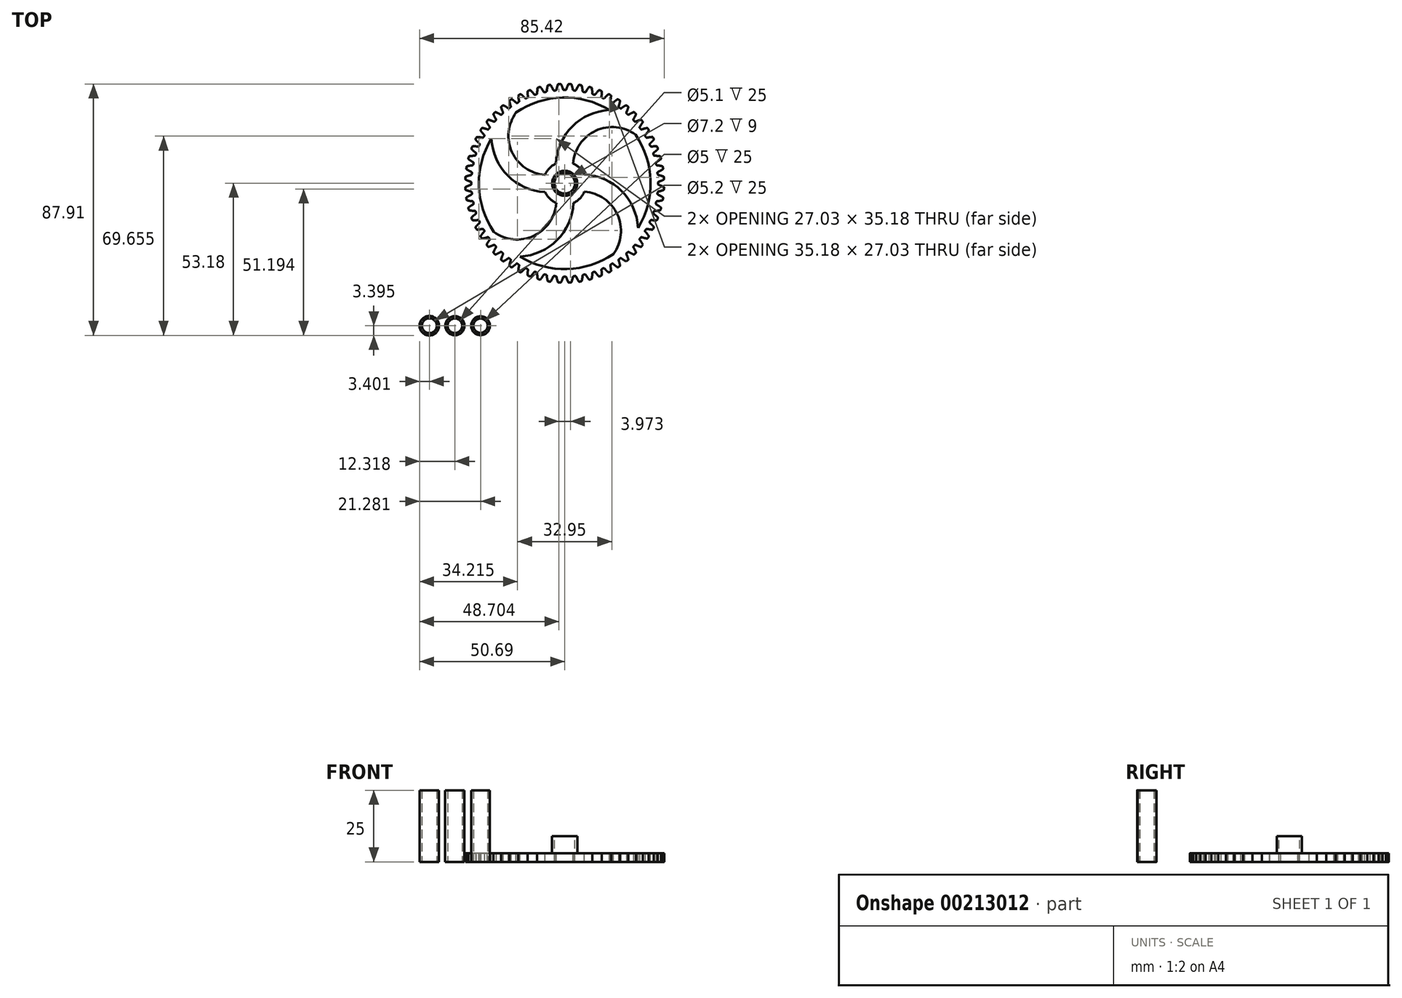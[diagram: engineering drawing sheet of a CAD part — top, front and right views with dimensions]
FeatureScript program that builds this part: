
annotation { "Feature Type Name" : "Feature", "Feature Type Description" : "" }
export const myFeature = defineFeature(function(context is Context, id is Id, definition is map)
    precondition{}
    {
        {
            var Q0;
            Q0=qCreatedBy(makeId("Top.planeOp"),FACE);
            var sketch = newSketch(context, id + "F0", { "sketchPlane" : qUnion([Q0])});
            skCircle(sketch, "E0", {"center": v(0, 0) * mm, "radius": 31.71 * mm, "construction": true});
            skLineSegment(sketch, "E1", {"start": v(0, 0) * mm, "end": v(31.71, 0) * mm, "construction": true});
            skLineSegment(sketch, "E2", {"start": v(31.71, 0) * mm, "end": v(31.71, 0) * mm});
            skLineSegment(sketch, "E3", {"start": v(0, 0) * mm, "end": v(31.68, 1.5) * mm, "construction": true});
            skLineSegment(sketch, "E4", {"start": v(31.68, 1.5) * mm, "end": v(31.75, 0) * mm, "construction": true});
            skLineSegment(sketch, "E5", {"start": v(0, 0) * mm, "end": v(31.57, 2.98) * mm, "construction": true});
            skLineSegment(sketch, "E6", {"start": v(31.57, 2.98) * mm, "end": v(31.86, 0) * mm, "construction": true});
            skLineSegment(sketch, "E7", {"start": v(0, 0) * mm, "end": v(31.4, 4.47) * mm, "construction": true});
            skLineSegment(sketch, "E8", {"start": v(31.4, 4.47) * mm, "end": v(32.03, 0.03) * mm, "construction": true});
            skLineSegment(sketch, "E9", {"start": v(0, 0) * mm, "end": v(31.15, 5.94) * mm, "construction": true});
            skLineSegment(sketch, "E10", {"start": v(31.15, 5.94) * mm, "end": v(32.27, 0.07) * mm, "construction": true});
            skLineSegment(sketch, "E11", {"start": v(0, 0) * mm, "end": v(30.84, 7.4) * mm, "construction": true});
            skLineSegment(sketch, "E12", {"start": v(30.84, 7.4) * mm, "end": v(32.58, 0.14) * mm, "construction": true});
            skLineSegment(sketch, "E13", {"start": v(0, 0) * mm, "end": v(30.46, 8.85) * mm, "construction": true});
            skLineSegment(sketch, "E14", {"start": v(30.46, 8.85) * mm, "end": v(32.96, 0.24) * mm, "construction": true});
            skLineSegment(sketch, "E15", {"start": v(0, 0) * mm, "end": v(30, 10.27) * mm, "construction": true});
            skLineSegment(sketch, "E16", {"start": v(30, 10.27) * mm, "end": v(33.4, 0.38) * mm, "construction": true});
            skLineSegment(sketch, "E17", {"start": v(0, 0) * mm, "end": v(29.49, 11.67) * mm, "construction": true});
            skLineSegment(sketch, "E18", {"start": v(29.49, 11.67) * mm, "end": v(33.89, 0.56) * mm, "construction": true});
            skLineSegment(sketch, "E19", {"start": v(0, 0) * mm, "end": v(28.9, 13.05) * mm, "construction": true});
            skLineSegment(sketch, "E20", {"start": v(28.9, 13.05) * mm, "end": v(34.44, 0.8) * mm, "construction": true});
            skLineSegment(sketch, "E21", {"start": v(0, 0) * mm, "end": v(28.26, 14.4) * mm, "construction": true});
            skLineSegment(sketch, "E22", {"start": v(28.26, 14.4) * mm, "end": v(35.04, 1.08) * mm, "construction": true});
            skPoint(sketch, "E23", {"position": v(31.71, 0) * mm});
            skCircle(sketch, "E24", {"center": v(0, 0) * mm, "radius": 32.62 * mm});
            skFitSpline(sketch, "E25", {"points": [v(31.71, 0) * mm, v(31.75, 0) * mm, v(31.86, 0) * mm, v(32.03, 0.03) * mm, v(32.27, 0.07) * mm, v(32.58, 0.14) * mm, v(32.96, 0.24) * mm, v(33.4, 0.38) * mm, v(33.89, 0.56) * mm, v(34.44, 0.8) * mm, v(35.04, 1.08) * mm], "startDerivative": vector(0.92, 0.02) * mm, "endDerivative": vector(4.16, 2.05) * mm, "construction": true});
            skFitSpline(sketch, "E26", {"points": [v(31.71, 0) * mm, v(31.75, 0) * mm, v(31.86, 0) * mm, v(32.03, 0.03) * mm, v(32.27, 0.07) * mm, v(32.58, 0.14) * mm, v(32.96, 0.24) * mm, v(33.4, 0.38) * mm, v(33.89, 0.56) * mm, v(34.44, 0.8) * mm, v(35.04, 1.08) * mm], "startDerivative": vector(0.92, 0.02) * mm, "endDerivative": vector(4.16, 2.05) * mm, "construction": true});
            skLineSegment(sketch, "E27", {"start": v(0, 0) * mm, "end": v(43.9, 1.8) * mm, "construction": true});
            skFitSpline(sketch, "E28", {"points": [v(31.71, 0) * mm, v(31.75, 0) * mm, v(31.86, 0) * mm, v(32.03, 0.03) * mm, v(32.27, 0.07) * mm, v(32.58, 0.14) * mm, v(32.96, 0.24) * mm, v(33.4, 0.38) * mm, v(33.89, 0.56) * mm, v(34.44, 0.8) * mm, v(35.04, 1.08) * mm], "startDerivative": vector(0.92, 0.02) * mm, "endDerivative": vector(4.16, 2.05) * mm});
            skFitSpline(sketch, "E29.MirrorCS", {"points": [v(31.6, 2.6) * mm, v(31.64, 2.6) * mm, v(31.75, 2.6) * mm, v(31.92, 2.6) * mm, v(32.17, 2.58) * mm, v(32.48, 2.54) * mm, v(32.87, 2.47) * mm, v(33.31, 2.37) * mm, v(33.82, 2.22) * mm, v(34.39, 2.04) * mm, v(35.01, 1.8) * mm], "startDerivative": vector(0.92, 0.06) * mm, "endDerivative": vector(4.32, -1.7) * mm});
            skArc(sketch, "E30", {"start": v(34.7, 1.92) * mm, "mid": v(-34.73, -1.43) * mm, "end": v(34.75, 0.94) * mm, "construction": true});
            skArc(sketch, "E31", {"start": v(34.75, 0.94) * mm, "mid": v(34.73, 1.43) * mm, "end": v(34.7, 1.92) * mm});
            skSolve(sketch);
        }
        {
            var Q0;
            Q0=qCreatedBy(makeId("Front.planeOp"),FACE);
            var sketch = newSketch(context, id + "F1", { "sketchPlane" : qUnion([Q0])});
            skLineSegment(sketch, "E32", {"start": v(0, 0) * mm, "end": v(0, 39.54) * mm});
            skSolve(sketch);
        }
        {
            var Q0;
            {var subQ0=sQuery(id+"F0.wireOp",EDGE,"E24");var subQ1=makeQuery(id+"F0.imprint","INTERSECT",VERTEX,{"derivedFrom":[subQ0,sQuery(id+"F0.wireOp",EDGE,"E28")]});Q0=makeQuery(id+"F0.imprint","IMPRINT",FACE,{"disambiguationData":[TD([[makeQuery(id+"F0.imprint","IMPRINT",EDGE,{"disambiguationData":[TD([[subQ1,-1.0]])],"derivedFrom":subQ0}),1.0]])]});}
            var Q1;
            {var subQ0=sQuery(id+"F0.wireOp",EDGE,"E28");Q1=makeQuery(id+"F0.imprint","IMPRINT",FACE,{"disambiguationData":[TD([[makeQuery(id+"F0.imprint","IMPRINT",EDGE,{"derivedFrom":subQ0}),1.0]])]});}
            extrude(context, id + "F2", {"entities" : qUnion([Q0, Q1]), "depth" : 3 * mm});
        }
        {
            var Q0;
            Q0=makeQuery(id+"F2.opExtrude","SWEPT_EDGE",EDGE,{"disambiguationData":[OSD([sQuery(id+"F0.wireOp",EDGE,"E24"),sQuery(id+"F0.wireOp",EDGE,"E28")])]});
            var Q1;
            Q1=makeQuery(id+"F2.opExtrude","SWEPT_EDGE",EDGE,{"disambiguationData":[OSD([sQuery(id+"F0.wireOp",EDGE,"E28"),sQuery(id+"F0.wireOp",EDGE,"E31")])]});
            var Q2;
            Q2=makeQuery(id+"F2.opExtrude","SWEPT_EDGE",EDGE,{"disambiguationData":[OSD([sQuery(id+"F0.wireOp",EDGE,"E29.MirrorCS"),sQuery(id+"F0.wireOp",EDGE,"E31")])]});
            var Q3;
            Q3=makeQuery(id+"F2.opExtrude","SWEPT_EDGE",EDGE,{"disambiguationData":[OSD([sQuery(id+"F0.wireOp",EDGE,"E24"),sQuery(id+"F0.wireOp",EDGE,"E29.MirrorCS")])]});
            fillet(context, id + "F3", {"entities" : qUnion([Q0, Q1, Q2, Q3]), "radius" : 0.4 * mm, "tangentPropagation" : true, "allowEdgeOverflow" : false});
        }
        {
            var Q0;
            Q0=makeQuery(id+"F2.opExtrude","SWEPT_BODY",BODY,{"disambiguationData":[OSD([sQuery(id+"F0.wireOp",EDGE,"E24"),sQuery(id+"F0.wireOp",EDGE,"E28"),sQuery(id+"F0.wireOp",EDGE,"E29.MirrorCS"),sQuery(id+"F0.wireOp",EDGE,"E31")])]});
            var Q1;
            Q1=sQuery(id+"F1.wireOp",EDGE,"E32");
            circularPattern(context, id + "F4", {"operationType" : NewBodyOperationType.ADD, "entities" : qUnion([Q0]), "axis" : qUnion([Q1]), "angle" : 360 * degree, "instanceCount" : 60, "equalSpace" : true});
        }
        {
            var Q0;
            {var subQ0=makeQuery(id+"F2.opExtrude","CAP_FACE",FACE,{"disambiguationData":[OSD([sQuery(id+"F0.wireOp",EDGE,"E24"),sQuery(id+"F0.wireOp",EDGE,"E28"),sQuery(id+"F0.wireOp",EDGE,"E29.MirrorCS"),sQuery(id+"F0.wireOp",EDGE,"E31")])],"isStart":false});Q0=makeQuery(id+"F4.boolean.opBoolean","MERGE",FACE,{"derivedFrom":[subQ0,makeQuery(id+"F4.opPattern","COPY",FACE,{"derivedFrom":subQ0,"instanceName":"1"}),makeQuery(id+"F4.opPattern","COPY",FACE,{"derivedFrom":subQ0,"instanceName":"2"}),makeQuery(id+"F4.opPattern","COPY",FACE,{"derivedFrom":subQ0,"instanceName":"3"}),makeQuery(id+"F4.opPattern","COPY",FACE,{"derivedFrom":subQ0,"instanceName":"4"}),makeQuery(id+"F4.opPattern","COPY",FACE,{"derivedFrom":subQ0,"instanceName":"5"}),makeQuery(id+"F4.opPattern","COPY",FACE,{"derivedFrom":subQ0,"instanceName":"6"}),makeQuery(id+"F4.opPattern","COPY",FACE,{"derivedFrom":subQ0,"instanceName":"7"}),makeQuery(id+"F4.opPattern","COPY",FACE,{"derivedFrom":subQ0,"instanceName":"8"}),makeQuery(id+"F4.opPattern","COPY",FACE,{"derivedFrom":subQ0,"instanceName":"9"}),makeQuery(id+"F4.opPattern","COPY",FACE,{"derivedFrom":subQ0,"instanceName":"10"}),makeQuery(id+"F4.opPattern","COPY",FACE,{"derivedFrom":subQ0,"instanceName":"11"}),makeQuery(id+"F4.opPattern","COPY",FACE,{"derivedFrom":subQ0,"instanceName":"12"}),makeQuery(id+"F4.opPattern","COPY",FACE,{"derivedFrom":subQ0,"instanceName":"13"}),makeQuery(id+"F4.opPattern","COPY",FACE,{"derivedFrom":subQ0,"instanceName":"14"}),makeQuery(id+"F4.opPattern","COPY",FACE,{"derivedFrom":subQ0,"instanceName":"15"}),makeQuery(id+"F4.opPattern","COPY",FACE,{"derivedFrom":subQ0,"instanceName":"16"}),makeQuery(id+"F4.opPattern","COPY",FACE,{"derivedFrom":subQ0,"instanceName":"17"}),makeQuery(id+"F4.opPattern","COPY",FACE,{"derivedFrom":subQ0,"instanceName":"18"}),makeQuery(id+"F4.opPattern","COPY",FACE,{"derivedFrom":subQ0,"instanceName":"19"}),makeQuery(id+"F4.opPattern","COPY",FACE,{"derivedFrom":subQ0,"instanceName":"20"}),makeQuery(id+"F4.opPattern","COPY",FACE,{"derivedFrom":subQ0,"instanceName":"21"}),makeQuery(id+"F4.opPattern","COPY",FACE,{"derivedFrom":subQ0,"instanceName":"22"}),makeQuery(id+"F4.opPattern","COPY",FACE,{"derivedFrom":subQ0,"instanceName":"23"}),makeQuery(id+"F4.opPattern","COPY",FACE,{"derivedFrom":subQ0,"instanceName":"24"}),makeQuery(id+"F4.opPattern","COPY",FACE,{"derivedFrom":subQ0,"instanceName":"25"}),makeQuery(id+"F4.opPattern","COPY",FACE,{"derivedFrom":subQ0,"instanceName":"26"}),makeQuery(id+"F4.opPattern","COPY",FACE,{"derivedFrom":subQ0,"instanceName":"27"}),makeQuery(id+"F4.opPattern","COPY",FACE,{"derivedFrom":subQ0,"instanceName":"28"}),makeQuery(id+"F4.opPattern","COPY",FACE,{"derivedFrom":subQ0,"instanceName":"29"}),makeQuery(id+"F4.opPattern","COPY",FACE,{"derivedFrom":subQ0,"instanceName":"30"}),makeQuery(id+"F4.opPattern","COPY",FACE,{"derivedFrom":subQ0,"instanceName":"31"}),makeQuery(id+"F4.opPattern","COPY",FACE,{"derivedFrom":subQ0,"instanceName":"32"}),makeQuery(id+"F4.opPattern","COPY",FACE,{"derivedFrom":subQ0,"instanceName":"33"}),makeQuery(id+"F4.opPattern","COPY",FACE,{"derivedFrom":subQ0,"instanceName":"34"}),makeQuery(id+"F4.opPattern","COPY",FACE,{"derivedFrom":subQ0,"instanceName":"35"}),makeQuery(id+"F4.opPattern","COPY",FACE,{"derivedFrom":subQ0,"instanceName":"36"}),makeQuery(id+"F4.opPattern","COPY",FACE,{"derivedFrom":subQ0,"instanceName":"37"}),makeQuery(id+"F4.opPattern","COPY",FACE,{"derivedFrom":subQ0,"instanceName":"38"}),makeQuery(id+"F4.opPattern","COPY",FACE,{"derivedFrom":subQ0,"instanceName":"39"}),makeQuery(id+"F4.opPattern","COPY",FACE,{"derivedFrom":subQ0,"instanceName":"40"}),makeQuery(id+"F4.opPattern","COPY",FACE,{"derivedFrom":subQ0,"instanceName":"41"}),makeQuery(id+"F4.opPattern","COPY",FACE,{"derivedFrom":subQ0,"instanceName":"42"}),makeQuery(id+"F4.opPattern","COPY",FACE,{"derivedFrom":subQ0,"instanceName":"43"}),makeQuery(id+"F4.opPattern","COPY",FACE,{"derivedFrom":subQ0,"instanceName":"44"}),makeQuery(id+"F4.opPattern","COPY",FACE,{"derivedFrom":subQ0,"instanceName":"45"}),makeQuery(id+"F4.opPattern","COPY",FACE,{"derivedFrom":subQ0,"instanceName":"46"}),makeQuery(id+"F4.opPattern","COPY",FACE,{"derivedFrom":subQ0,"instanceName":"47"}),makeQuery(id+"F4.opPattern","COPY",FACE,{"derivedFrom":subQ0,"instanceName":"48"}),makeQuery(id+"F4.opPattern","COPY",FACE,{"derivedFrom":subQ0,"instanceName":"49"}),makeQuery(id+"F4.opPattern","COPY",FACE,{"derivedFrom":subQ0,"instanceName":"50"}),makeQuery(id+"F4.opPattern","COPY",FACE,{"derivedFrom":subQ0,"instanceName":"51"}),makeQuery(id+"F4.opPattern","COPY",FACE,{"derivedFrom":subQ0,"instanceName":"52"}),makeQuery(id+"F4.opPattern","COPY",FACE,{"derivedFrom":subQ0,"instanceName":"53"}),makeQuery(id+"F4.opPattern","COPY",FACE,{"derivedFrom":subQ0,"instanceName":"54"}),makeQuery(id+"F4.opPattern","COPY",FACE,{"derivedFrom":subQ0,"instanceName":"55"}),makeQuery(id+"F4.opPattern","COPY",FACE,{"derivedFrom":subQ0,"instanceName":"56"}),makeQuery(id+"F4.opPattern","COPY",FACE,{"derivedFrom":subQ0,"instanceName":"57"}),makeQuery(id+"F4.opPattern","COPY",FACE,{"derivedFrom":subQ0,"instanceName":"58"}),makeQuery(id+"F4.opPattern","COPY",FACE,{"derivedFrom":subQ0,"instanceName":"59"})]});}
            var sketch = newSketch(context, id + "F5", { "sketchPlane" : qUnion([Q0])});
            skCircle(sketch, "E33", {"center": v(0, 0) * mm, "radius": 4.4 * mm});
            skLineSegment(sketch, "E34", {"start": v(0, 0) * mm, "end": v(32.62, -0.37) * mm, "construction": true});
            skCircle(sketch, "E35", {"center": v(0, 0) * mm, "radius": 7.5 * mm});
            skCircle(sketch, "E36", {"center": v(0, 0) * mm, "radius": 30 * mm});
            skSolve(sketch);
        }
        {
            var Q0;
            Q0=makeQuery(id+"F5.imprint","IMPRINT",FACE,{"disambiguationData":[TD([[makeQuery(id+"F5.imprint","IMPRINT",EDGE,{"derivedFrom":sQuery(id+"F5.wireOp",EDGE,"E33")}),1.0]])]});
            extrude(context, id + "F6", {"entities" : qUnion([Q0]), "operationType" : NewBodyOperationType.ADD, "depth" : 6 * mm});
        }
        {
            var Q0;
            Q0=makeQuery(id+"F2.opExtrude","SWEPT_BODY",BODY,{"disambiguationData":[OSD([sQuery(id+"F0.wireOp",EDGE,"E24"),sQuery(id+"F0.wireOp",EDGE,"E28"),sQuery(id+"F0.wireOp",EDGE,"E29.MirrorCS"),sQuery(id+"F0.wireOp",EDGE,"E31")])]});
            var Q1;
            Q1=sQuery(id+"F1.wireOp",EDGE,"E32");
            transform(context, id + "F7", {"entities" : qUnion([Q0]), "transformType" : TransformType.ROTATION, "transformAxis" : qUnion([Q1]), "angle" : 0.65 * degree, "makeCopy" : false});
        }
        {
            var Q0;
            Q0=makeQuery(id+"F6.opExtrude","CAP_FACE",FACE,{"disambiguationData":[OSD([sQuery(id+"F5.wireOp",EDGE,"E33")])],"isStart":false});
            var sketch = newSketch(context, id + "F8", { "sketchPlane" : qUnion([Q0])});
            skCircle(sketch, "E37", {"center": v(0, 0) * mm, "radius": 3.6 * mm});
            skSolve(sketch);
        }
        {
            var Q0;
            Q0=makeQuery(id+"F8.imprint","IMPRINT",FACE,{"disambiguationData":[TD([[makeQuery(id+"F8.imprint","IMPRINT",EDGE,{"derivedFrom":sQuery(id+"F8.wireOp",EDGE,"E37")}),1.0]])]});
            extrude(context, id + "F9", {"entities" : qUnion([Q0]), "operationType" : NewBodyOperationType.REMOVE, "endBound" : BoundingType.UP_TO_NEXT, "oppositeDirection" : true, "depth" : 25 * mm});
        }
        {
            var Q0;
            {var subQ0=makeQuery(id+"F2.opExtrude","CAP_FACE",FACE,{"disambiguationData":[OSD([sQuery(id+"F0.wireOp",EDGE,"E24"),sQuery(id+"F0.wireOp",EDGE,"E28"),sQuery(id+"F0.wireOp",EDGE,"E29.MirrorCS"),sQuery(id+"F0.wireOp",EDGE,"E31")])],"isStart":false});Q0=makeQuery(id+"F4.boolean.opBoolean","MERGE",FACE,{"derivedFrom":[subQ0,makeQuery(id+"F4.opPattern","COPY",FACE,{"derivedFrom":subQ0,"instanceName":"1"}),makeQuery(id+"F4.opPattern","COPY",FACE,{"derivedFrom":subQ0,"instanceName":"2"}),makeQuery(id+"F4.opPattern","COPY",FACE,{"derivedFrom":subQ0,"instanceName":"3"}),makeQuery(id+"F4.opPattern","COPY",FACE,{"derivedFrom":subQ0,"instanceName":"4"}),makeQuery(id+"F4.opPattern","COPY",FACE,{"derivedFrom":subQ0,"instanceName":"5"}),makeQuery(id+"F4.opPattern","COPY",FACE,{"derivedFrom":subQ0,"instanceName":"6"}),makeQuery(id+"F4.opPattern","COPY",FACE,{"derivedFrom":subQ0,"instanceName":"7"}),makeQuery(id+"F4.opPattern","COPY",FACE,{"derivedFrom":subQ0,"instanceName":"8"}),makeQuery(id+"F4.opPattern","COPY",FACE,{"derivedFrom":subQ0,"instanceName":"9"}),makeQuery(id+"F4.opPattern","COPY",FACE,{"derivedFrom":subQ0,"instanceName":"10"}),makeQuery(id+"F4.opPattern","COPY",FACE,{"derivedFrom":subQ0,"instanceName":"11"}),makeQuery(id+"F4.opPattern","COPY",FACE,{"derivedFrom":subQ0,"instanceName":"12"}),makeQuery(id+"F4.opPattern","COPY",FACE,{"derivedFrom":subQ0,"instanceName":"13"}),makeQuery(id+"F4.opPattern","COPY",FACE,{"derivedFrom":subQ0,"instanceName":"14"}),makeQuery(id+"F4.opPattern","COPY",FACE,{"derivedFrom":subQ0,"instanceName":"15"}),makeQuery(id+"F4.opPattern","COPY",FACE,{"derivedFrom":subQ0,"instanceName":"16"}),makeQuery(id+"F4.opPattern","COPY",FACE,{"derivedFrom":subQ0,"instanceName":"17"}),makeQuery(id+"F4.opPattern","COPY",FACE,{"derivedFrom":subQ0,"instanceName":"18"}),makeQuery(id+"F4.opPattern","COPY",FACE,{"derivedFrom":subQ0,"instanceName":"19"}),makeQuery(id+"F4.opPattern","COPY",FACE,{"derivedFrom":subQ0,"instanceName":"20"}),makeQuery(id+"F4.opPattern","COPY",FACE,{"derivedFrom":subQ0,"instanceName":"21"}),makeQuery(id+"F4.opPattern","COPY",FACE,{"derivedFrom":subQ0,"instanceName":"22"}),makeQuery(id+"F4.opPattern","COPY",FACE,{"derivedFrom":subQ0,"instanceName":"23"}),makeQuery(id+"F4.opPattern","COPY",FACE,{"derivedFrom":subQ0,"instanceName":"24"}),makeQuery(id+"F4.opPattern","COPY",FACE,{"derivedFrom":subQ0,"instanceName":"25"}),makeQuery(id+"F4.opPattern","COPY",FACE,{"derivedFrom":subQ0,"instanceName":"26"}),makeQuery(id+"F4.opPattern","COPY",FACE,{"derivedFrom":subQ0,"instanceName":"27"}),makeQuery(id+"F4.opPattern","COPY",FACE,{"derivedFrom":subQ0,"instanceName":"28"}),makeQuery(id+"F4.opPattern","COPY",FACE,{"derivedFrom":subQ0,"instanceName":"29"}),makeQuery(id+"F4.opPattern","COPY",FACE,{"derivedFrom":subQ0,"instanceName":"30"}),makeQuery(id+"F4.opPattern","COPY",FACE,{"derivedFrom":subQ0,"instanceName":"31"}),makeQuery(id+"F4.opPattern","COPY",FACE,{"derivedFrom":subQ0,"instanceName":"32"}),makeQuery(id+"F4.opPattern","COPY",FACE,{"derivedFrom":subQ0,"instanceName":"33"}),makeQuery(id+"F4.opPattern","COPY",FACE,{"derivedFrom":subQ0,"instanceName":"34"}),makeQuery(id+"F4.opPattern","COPY",FACE,{"derivedFrom":subQ0,"instanceName":"35"}),makeQuery(id+"F4.opPattern","COPY",FACE,{"derivedFrom":subQ0,"instanceName":"36"}),makeQuery(id+"F4.opPattern","COPY",FACE,{"derivedFrom":subQ0,"instanceName":"37"}),makeQuery(id+"F4.opPattern","COPY",FACE,{"derivedFrom":subQ0,"instanceName":"38"}),makeQuery(id+"F4.opPattern","COPY",FACE,{"derivedFrom":subQ0,"instanceName":"39"}),makeQuery(id+"F4.opPattern","COPY",FACE,{"derivedFrom":subQ0,"instanceName":"40"}),makeQuery(id+"F4.opPattern","COPY",FACE,{"derivedFrom":subQ0,"instanceName":"41"}),makeQuery(id+"F4.opPattern","COPY",FACE,{"derivedFrom":subQ0,"instanceName":"42"}),makeQuery(id+"F4.opPattern","COPY",FACE,{"derivedFrom":subQ0,"instanceName":"43"}),makeQuery(id+"F4.opPattern","COPY",FACE,{"derivedFrom":subQ0,"instanceName":"44"}),makeQuery(id+"F4.opPattern","COPY",FACE,{"derivedFrom":subQ0,"instanceName":"45"}),makeQuery(id+"F4.opPattern","COPY",FACE,{"derivedFrom":subQ0,"instanceName":"46"}),makeQuery(id+"F4.opPattern","COPY",FACE,{"derivedFrom":subQ0,"instanceName":"47"}),makeQuery(id+"F4.opPattern","COPY",FACE,{"derivedFrom":subQ0,"instanceName":"48"}),makeQuery(id+"F4.opPattern","COPY",FACE,{"derivedFrom":subQ0,"instanceName":"49"}),makeQuery(id+"F4.opPattern","COPY",FACE,{"derivedFrom":subQ0,"instanceName":"50"}),makeQuery(id+"F4.opPattern","COPY",FACE,{"derivedFrom":subQ0,"instanceName":"51"}),makeQuery(id+"F4.opPattern","COPY",FACE,{"derivedFrom":subQ0,"instanceName":"52"}),makeQuery(id+"F4.opPattern","COPY",FACE,{"derivedFrom":subQ0,"instanceName":"53"}),makeQuery(id+"F4.opPattern","COPY",FACE,{"derivedFrom":subQ0,"instanceName":"54"}),makeQuery(id+"F4.opPattern","COPY",FACE,{"derivedFrom":subQ0,"instanceName":"55"}),makeQuery(id+"F4.opPattern","COPY",FACE,{"derivedFrom":subQ0,"instanceName":"56"}),makeQuery(id+"F4.opPattern","COPY",FACE,{"derivedFrom":subQ0,"instanceName":"57"}),makeQuery(id+"F4.opPattern","COPY",FACE,{"derivedFrom":subQ0,"instanceName":"58"}),makeQuery(id+"F4.opPattern","COPY",FACE,{"derivedFrom":subQ0,"instanceName":"59"})]});}
            var sketch = newSketch(context, id + "F10", { "sketchPlane" : qUnion([Q0])});
            skCircle(sketch, "E38", {"center": v(0, 0) * mm, "radius": 7.5 * mm});
            skCircle(sketch, "E39", {"center": v(0, 0) * mm, "radius": 30 * mm});
            skPoint(sketch, "E40.first.point", {"position": v(0, 7.5) * mm});
            skPoint(sketch, "E40.second.point", {"position": v(5.9, 18.75) * mm});
            skPoint(sketch, "E40.third.point", {"position": v(20.09, 22.28) * mm});
            skArc(sketch, "E41", {"start": v(24.74, 16.97) * mm, "mid": v(10.87, 18.38) * mm, "end": v(2.96, 6.9) * mm});
            skArc(sketch, "E42", {"start": v(20.09, 22.28) * mm, "mid": v(6.72, 19.4) * mm, "end": v(0, 7.5) * mm, "construction": true});
            skArc(sketch, "E43", {"start": v(15.6, 25.62) * mm, "mid": v(2.65, 19.84) * mm, "end": v(-3.05, 6.85) * mm});
            skArc(sketch, "E44.1.0", {"start": v(-16.97, 24.74) * mm, "mid": v(-18.38, 10.87) * mm, "end": v(-6.9, 2.96) * mm});
            skArc(sketch, "E44.1.1", {"start": v(-25.62, 15.6) * mm, "mid": v(-19.84, 2.65) * mm, "end": v(-6.85, -3.05) * mm});
            skArc(sketch, "E44.2.0", {"start": v(-24.74, -16.97) * mm, "mid": v(-10.87, -18.38) * mm, "end": v(-2.96, -6.9) * mm});
            skArc(sketch, "E44.2.1", {"start": v(-15.6, -25.62) * mm, "mid": v(-2.65, -19.84) * mm, "end": v(3.05, -6.85) * mm});
            skArc(sketch, "E44.3.0", {"start": v(16.97, -24.74) * mm, "mid": v(18.38, -10.87) * mm, "end": v(6.9, -2.96) * mm});
            skArc(sketch, "E44.3.1", {"start": v(25.62, -15.6) * mm, "mid": v(19.84, -2.65) * mm, "end": v(6.85, 3.05) * mm});
            skLineSegment(sketch, "E45", {"start": v(0, 0) * mm, "end": v(20.09, 22.28) * mm, "construction": true});
            skSolve(sketch);
        }
        {
            var Q0;
            {var subQ0=sQuery(id+"F10.wireOp",EDGE,"E44.2.1");Q0=makeQuery(id+"F10.imprint","IMPRINT",FACE,{"disambiguationData":[TD([[makeQuery(id+"F10.imprint","IMPRINT",EDGE,{"derivedFrom":subQ0}),-1.0]])]});}
            var Q1;
            {var subQ0=sQuery(id+"F10.wireOp",EDGE,"E44.1.1");Q1=makeQuery(id+"F10.imprint","IMPRINT",FACE,{"disambiguationData":[TD([[makeQuery(id+"F10.imprint","IMPRINT",EDGE,{"derivedFrom":subQ0}),-1.0]])]});}
            var Q2;
            {var subQ0=sQuery(id+"F10.wireOp",EDGE,"E41");Q2=makeQuery(id+"F10.imprint","IMPRINT",FACE,{"disambiguationData":[TD([[makeQuery(id+"F10.imprint","IMPRINT",EDGE,{"derivedFrom":subQ0}),1.0]])]});}
            var Q3;
            {var subQ0=sQuery(id+"F10.wireOp",EDGE,"E43");Q3=makeQuery(id+"F10.imprint","IMPRINT",FACE,{"disambiguationData":[TD([[makeQuery(id+"F10.imprint","IMPRINT",EDGE,{"derivedFrom":subQ0}),-1.0]])]});}
            extrude(context, id + "F11", {"entities" : qUnion([Q0, Q1, Q2, Q3]), "operationType" : NewBodyOperationType.REMOVE, "endBound" : BoundingType.UP_TO_NEXT, "oppositeDirection" : true, "depth" : 25 * mm});
        }
        {
            var Q0;
            Q0=qCreatedBy(makeId("Top.planeOp"),FACE);
            var sketch = newSketch(context, id + "F12", { "sketchPlane" : qUnion([Q0])});
            skCircle(sketch, "E46", {"center": v(-47.29, -49.78) * mm, "radius": 2.6 * mm});
            skCircle(sketch, "E47", {"center": v(-47.29, -49.78) * mm, "radius": 3.4 * mm});
            skCircle(sketch, "E48", {"center": v(-38.37, -49.78) * mm, "radius": 2.55 * mm});
            skCircle(sketch, "E49", {"center": v(-38.37, -49.78) * mm, "radius": 3.35 * mm});
            skCircle(sketch, "E50", {"center": v(-29.4, -49.78) * mm, "radius": 2.5 * mm});
            skCircle(sketch, "E51", {"center": v(-29.4, -49.78) * mm, "radius": 3.3 * mm});
            skSolve(sketch);
        }
        {
            var Q0;
            Q0=makeQuery(id+"F12.imprint","IMPRINT",FACE,{"disambiguationData":[TD([[makeQuery(id+"F12.imprint","IMPRINT",EDGE,{"derivedFrom":sQuery(id+"F12.wireOp",EDGE,"E46")}),-1.0]])]});
            var Q1;
            Q1=makeQuery(id+"F12.imprint","IMPRINT",FACE,{"disambiguationData":[TD([[makeQuery(id+"F12.imprint","IMPRINT",EDGE,{"derivedFrom":sQuery(id+"F12.wireOp",EDGE,"E48")}),-1.0]])]});
            var Q2;
            Q2=makeQuery(id+"F12.imprint","IMPRINT",FACE,{"disambiguationData":[TD([[makeQuery(id+"F12.imprint","IMPRINT",EDGE,{"derivedFrom":sQuery(id+"F12.wireOp",EDGE,"E50")}),-1.0]])]});
            extrude(context, id + "F13", {"entities" : qUnion([Q0, Q1, Q2]), "depth" : 25 * mm});
        }
    });
